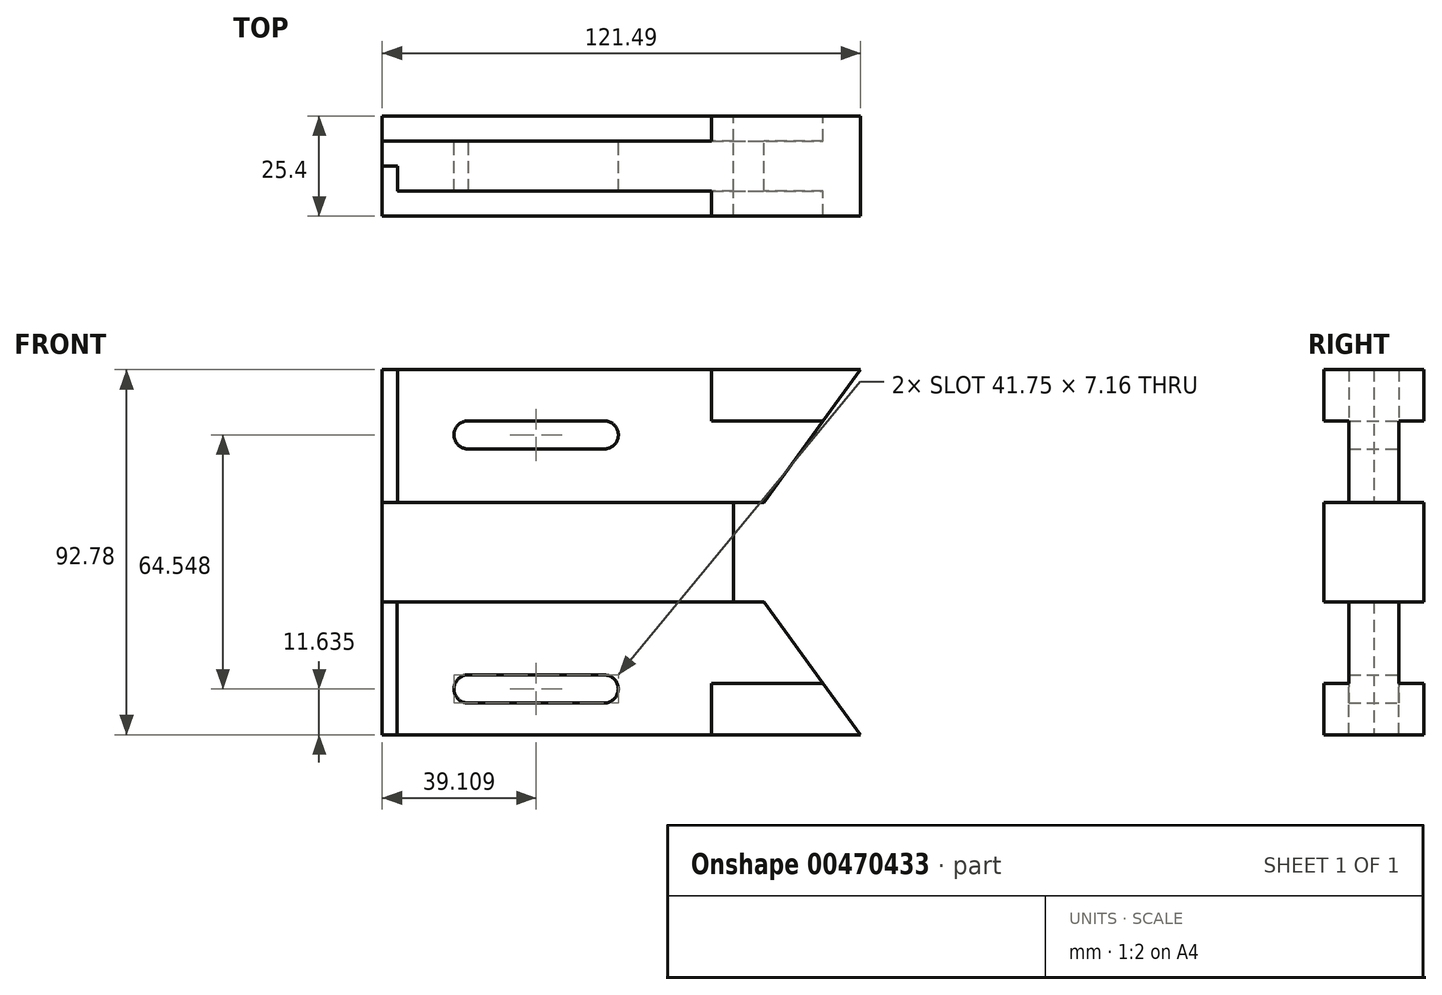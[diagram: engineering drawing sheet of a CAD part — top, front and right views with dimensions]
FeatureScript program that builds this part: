
annotation { "Feature Type Name" : "Feature", "Feature Type Description" : "" }
export const myFeature = defineFeature(function(context is Context, id is Id, definition is map)
    precondition{}
    {
        {
            var Q0;
            Q0=qCreatedBy(makeId("Front.planeOp"),FACE);
            var sketch = newSketch(context, id + "F0", { "sketchPlane" : qUnion([Q0])});
            skLineSegment(sketch, "E0", {"start": v(-67.14, 59) * mm, "end": v(-67.14, 25.24) * mm});
            skLineSegment(sketch, "E1", {"start": v(-67.14, 25.24) * mm, "end": v(54.35, 25.24) * mm});
            skLineSegment(sketch, "E2", {"start": v(54.35, 25.24) * mm, "end": v(54.35, 59) * mm});
            skLineSegment(sketch, "E3", {"start": v(54.35, 59) * mm, "end": v(-67.14, 59) * mm});
            skLineSegment(sketch, "E4", {"start": v(-63.22, 59) * mm, "end": v(-63.22, 25.24) * mm});
            skLineSegment(sketch, "E5", {"start": v(-67.14, 25.24) * mm, "end": v(-67.14, 12.62) * mm});
            skLineSegment(sketch, "E6", {"start": v(-67.14, 12.62) * mm, "end": v(22.15, 12.62) * mm});
            skLineSegment(sketch, "E7", {"start": v(22.15, 12.62) * mm, "end": v(22.15, 25.24) * mm});
            skLineSegment(sketch, "E8", {"start": v(16.53, 59) * mm, "end": v(16.53, 46) * mm});
            skLineSegment(sketch, "E9", {"start": v(54.35, 59) * mm, "end": v(29.82, 25.24) * mm});
            skLineSegment(sketch, "E10", {"start": v(16.53, 46) * mm, "end": v(44.9, 46) * mm});
            skArc(sketch, "E11", {"start": v(-45.22, 45.99) * mm, "mid": v(-48.9, 42.46) * mm, "end": v(-45.33, 38.83) * mm});
            skArc(sketch, "E12", {"start": v(-10.74, 38.83) * mm, "mid": v(-7.16, 42.41) * mm, "end": v(-10.74, 46) * mm});
            skLineSegment(sketch, "E13", {"start": v(-45.22, 45.99) * mm, "end": v(-10.74, 46) * mm});
            skLineSegment(sketch, "E14", {"start": v(-45.33, 38.83) * mm, "end": v(-10.74, 38.83) * mm});
            skLineSegment(sketch, "E15", {"start": v(-67.14, 12.62) * mm, "end": v(-67.14, 0) * mm});
            skLineSegment(sketch, "E16", {"start": v(-67.14, 0) * mm, "end": v(22.15, 0) * mm});
            skLineSegment(sketch, "E17", {"start": v(22.15, 0) * mm, "end": v(22.15, 12.62) * mm});
            skLineSegment(sketch, "E18", {"start": v(-67.14, 0) * mm, "end": v(-67.14, -33.77) * mm});
            skLineSegment(sketch, "E19", {"start": v(-67.14, -33.77) * mm, "end": v(-63.39, -33.77) * mm});
            skLineSegment(sketch, "E20", {"start": v(-63.39, -33.77) * mm, "end": v(-63.39, 0) * mm});
            skLineSegment(sketch, "E21", {"start": v(-63.39, -33.77) * mm, "end": v(54.35, -33.77) * mm});
            skPoint(sketch, "E21.endSnap0", {"position": v(-65.26, -33.77) * mm});
            skLineSegment(sketch, "E22", {"start": v(54.35, -33.77) * mm, "end": v(54.35, 0) * mm});
            skLineSegment(sketch, "E23", {"start": v(54.35, 0) * mm, "end": v(22.15, 0) * mm});
            skLineSegment(sketch, "E24", {"start": v(54.35, -33.77) * mm, "end": v(29.82, 0) * mm});
            skLineSegment(sketch, "E25", {"start": v(16.53, -33.77) * mm, "end": v(16.53, -20.75) * mm});
            skLineSegment(sketch, "E26", {"start": v(16.53, -20.75) * mm, "end": v(44.9, -20.75) * mm});
            skArc(sketch, "E27", {"start": v(-45.33, -18.56) * mm, "mid": v(-48.9, -22.14) * mm, "end": v(-45.31, -25.71) * mm});
            skArc(sketch, "E28", {"start": v(-10.74, -25.71) * mm, "mid": v(-7.16, -22.14) * mm, "end": v(-10.74, -18.56) * mm});
            skLineSegment(sketch, "E29", {"start": v(-45.33, -18.56) * mm, "end": v(-10.74, -18.56) * mm});
            skLineSegment(sketch, "E30", {"start": v(-45.34, -25.71) * mm, "end": v(-10.74, -25.71) * mm});
            skSolve(sketch);
        }
        {
            var Q0;
            {var subQ0=sQuery(id+"F0.wireOp",EDGE,"E5");Q0=makeQuery(id+"F0.imprint","IMPRINT",FACE,{"disambiguationData":[TD([[makeQuery(id+"F0.imprint","IMPRINT",EDGE,{"derivedFrom":subQ0}),1.0]])]});}
            var Q1;
            Q1=makeQuery(id+"F0.imprint","IMPRINT",FACE,{"disambiguationData":[TD([[makeQuery(id+"F0.imprint","IMPRINT",EDGE,{"derivedFrom":sQuery(id+"F0.wireOp",EDGE,"E6")}),-1.0]])]});
            extrude(context, id + "F1", {"entities" : qUnion([Q0, Q1]), "depth" : 25.4 * mm, "symmetric" : true});
        }
        {
            var Q0;
            {var subQ5=sQuery(id+"F0.wireOp",EDGE,"E4");Q0=makeQuery(id+"F0.imprint","IMPRINT",FACE,{"disambiguationData":[TD([[makeQuery(id+"F0.imprint","IMPRINT",EDGE,{"derivedFrom":subQ5}),1.0]])]});}
            var Q1;
            {var subQ8=sQuery(id+"F0.wireOp",EDGE,"E20");Q1=makeQuery(id+"F0.imprint","IMPRINT",FACE,{"disambiguationData":[TD([[makeQuery(id+"F0.imprint","IMPRINT",EDGE,{"derivedFrom":subQ8}),-1.0]])]});}
            extrude(context, id + "F2", {"entities" : qUnion([Q0, Q1]), "operationType" : NewBodyOperationType.ADD, "depth" : 12.7 * mm, "symmetric" : true});
        }
        {
            var Q0;
            {var subQ3=sQuery(id+"F0.wireOp",EDGE,"E8");Q0=makeQuery(id+"F0.imprint","IMPRINT",FACE,{"disambiguationData":[TD([[makeQuery(id+"F0.imprint","IMPRINT",EDGE,{"derivedFrom":subQ3}),1.0]])]});}
            var Q1;
            {var subQ3=sQuery(id+"F0.wireOp",EDGE,"E25");Q1=makeQuery(id+"F0.imprint","IMPRINT",FACE,{"disambiguationData":[TD([[makeQuery(id+"F0.imprint","IMPRINT",EDGE,{"derivedFrom":subQ3}),-1.0]])]});}
            extrude(context, id + "F3", {"entities" : qUnion([Q0, Q1]), "operationType" : NewBodyOperationType.ADD, "depth" : 25.4 * mm, "symmetric" : true});
        }
        {
            var Q0;
            {var subQ0=sQuery(id+"F0.wireOp",EDGE,"E0");Q0=makeQuery(id+"F0.imprint","IMPRINT",FACE,{"disambiguationData":[TD([[makeQuery(id+"F0.imprint","IMPRINT",EDGE,{"derivedFrom":subQ0}),1.0]])]});}
            var Q1;
            {var subQ0=sQuery(id+"F0.wireOp",EDGE,"E18");Q1=makeQuery(id+"F0.imprint","IMPRINT",FACE,{"disambiguationData":[TD([[makeQuery(id+"F0.imprint","IMPRINT",EDGE,{"derivedFrom":subQ0}),1.0]])]});}
            extrude(context, id + "F4", {"entities" : qUnion([Q0, Q1]), "operationType" : NewBodyOperationType.ADD, "oppositeDirection" : true, "depth" : 6.35 * mm});
        }
    });
